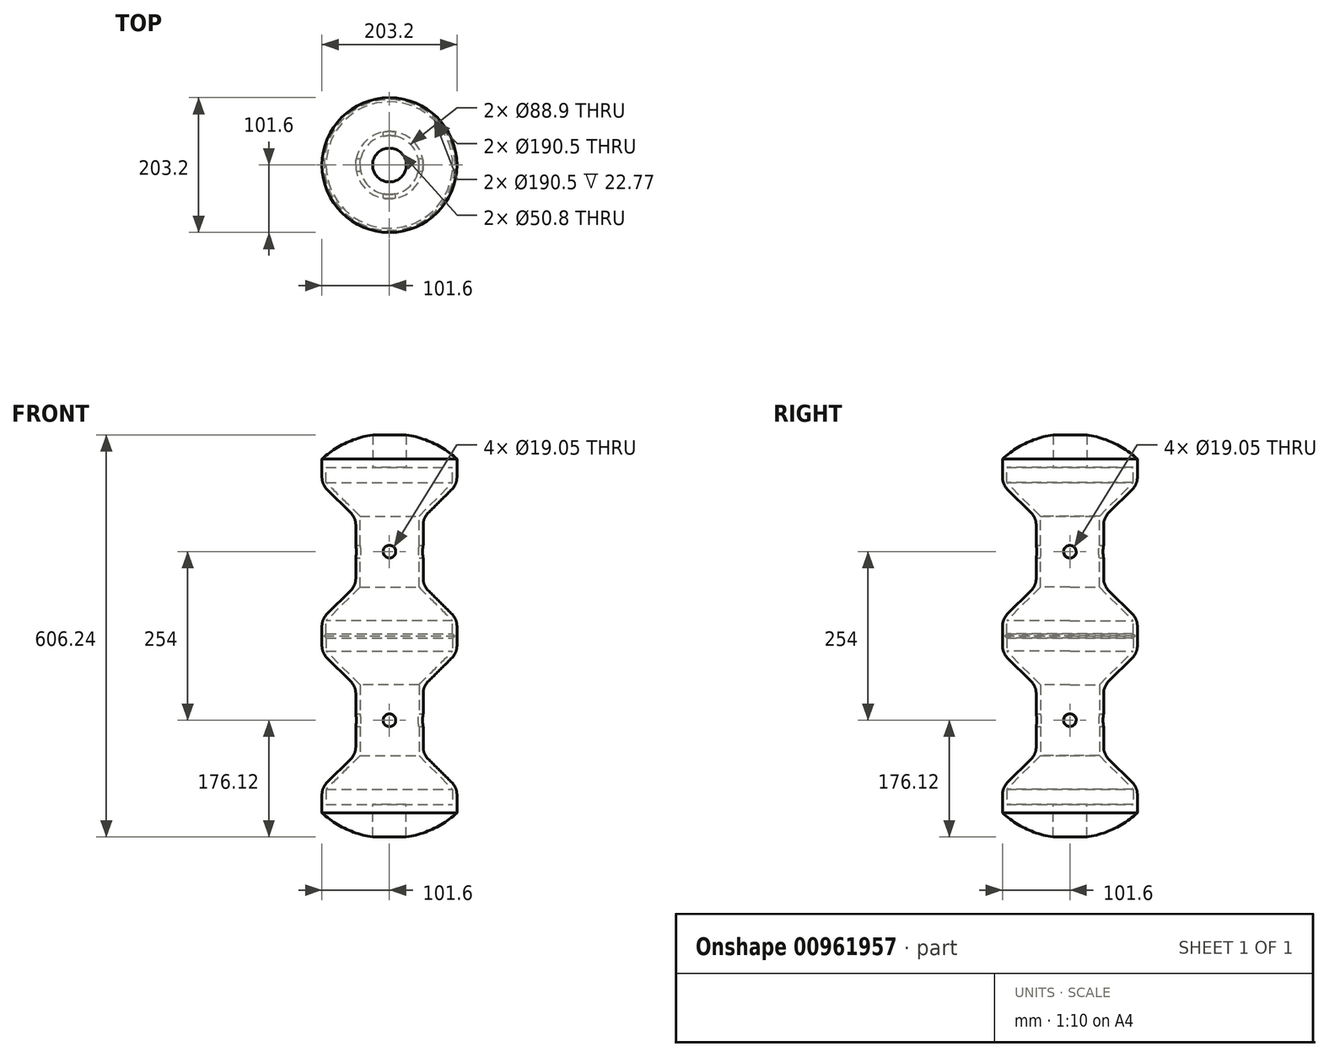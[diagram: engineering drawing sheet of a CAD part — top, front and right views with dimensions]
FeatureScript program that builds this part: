
annotation { "Feature Type Name" : "Feature", "Feature Type Description" : "" }
export const myFeature = defineFeature(function(context is Context, id is Id, definition is map)
    precondition{}
    {
        {
            var Q0;
            Q0=qCreatedBy(makeId("Front.planeOp"),FACE);
            var sketch = newSketch(context, id + "F0", { "sketchPlane" : qUnion([Q0])});
            skLineSegment(sketch, "E0", {"start": v(0, 0) * mm, "end": v(0, 254) * mm});
            skLineSegment(sketch, "E1", {"start": v(0, 254) * mm, "end": v(-101.6, 254) * mm});
            skLineSegment(sketch, "E2", {"start": v(-101.6, 254) * mm, "end": v(-101.6, 228.6) * mm});
            skLineSegment(sketch, "E3", {"start": v(-101.6, 228.6) * mm, "end": v(-50.8, 177.8) * mm});
            skLineSegment(sketch, "E4", {"start": v(0, 127) * mm, "end": v(39.45, 127) * mm, "construction": true});
            skLineSegment(sketch, "E5.MirrorCS", {"start": v(-101.6, 0) * mm, "end": v(-101.6, 25.4) * mm});
            skLineSegment(sketch, "E6.MirrorCS", {"start": v(-101.6, 25.4) * mm, "end": v(-50.8, 76.2) * mm});
            skLineSegment(sketch, "E7.MirrorCS", {"start": v(0, 0) * mm, "end": v(-101.6, 0) * mm});
            skLineSegment(sketch, "E8", {"start": v(-50.8, 177.8) * mm, "end": v(-50.8, 76.2) * mm});
            skSolve(sketch);
        }
        {
            var Q0;
            Q0=makeQuery(id+"F0.imprint","IMPRINT",FACE,{"disambiguationData":[TD([[makeQuery(id+"F0.imprint","IMPRINT",EDGE,{"derivedFrom":sQuery(id+"F0.wireOp",EDGE,"E0")}),1.0]])]});
            var Q1;
            Q1=sQuery(id+"F0.wireOp",EDGE,"E0");
            revolve(context, id + "F1", {"surfaceOperationType" : NewSurfaceOperationType.NEW, "entities" : qUnion([Q0]), "axis" : qUnion([Q1]), "revolveType" : RevolveType.FULL});
        }
        {
            var Q0;
            Q0=makeQuery(id+"F1.opRevolve","SWEPT_FACE",FACE,{"disambiguationData":[OSD([sQuery(id+"F0.wireOp",EDGE,"E1")])]});
            var Q1;
            Q1=makeQuery(id+"F1.opRevolve","SWEPT_BODY",BODY,{"disambiguationData":[OSD([sQuery(id+"F0.wireOp",EDGE,"E0"),sQuery(id+"F0.wireOp",EDGE,"E1"),sQuery(id+"F0.wireOp",EDGE,"E2"),sQuery(id+"F0.wireOp",EDGE,"E3"),sQuery(id+"F0.wireOp",EDGE,"E5.MirrorCS"),sQuery(id+"F0.wireOp",EDGE,"E6.MirrorCS"),sQuery(id+"F0.wireOp",EDGE,"E7.MirrorCS"),sQuery(id+"F0.wireOp",EDGE,"E8")])]});
            shell(context, id + "F2", {"entities" : qUnion([Q0]), "parts" : qUnion([Q1]), "thickness" : 6.35 * mm});
        }
        {
            var Q0;
            Q0=makeQuery(id+"F1.opRevolve","SWEPT_FACE",FACE,{"disambiguationData":[OSD([sQuery(id+"F0.wireOp",EDGE,"E7.MirrorCS")])]});
            var sketch = newSketch(context, id + "F3", { "sketchPlane" : qUnion([Q0])});
            skCircle(sketch, "E9", {"center": v(0, 0) * mm, "radius": 95.25 * mm});
            skSolve(sketch);
        }
        {
            var Q0;
            Q0 = qSketchRegion(id + "F3", true);
            extrude(context, id + "F4", {"entities" : qUnion([Q0]), "operationType" : NewBodyOperationType.REMOVE, "oppositeDirection" : true, "depth" : 6.35 * mm, "offsetDistance" : 25.4 * mm});
        }
        {
            var Q0;
            Q0=qCreatedBy(makeId("Right.planeOp"),FACE);
            var sketch = newSketch(context, id + "F5", { "sketchPlane" : qUnion([Q0])});
            skCircle(sketch, "E10", {"center": v(0, 127) * mm, "radius": 9.53 * mm});
            skSolve(sketch);
        }
        {
            var Q0;
            Q0 = qSketchRegion(id + "F5", true);
            extrude(context, id + "F6", {"entities" : qUnion([Q0]), "operationType" : NewBodyOperationType.REMOVE, "endBound" : BoundingType.SYMMETRIC, "oppositeDirection" : true, "depth" : 254 * mm, "offsetDistance" : 25.4 * mm});
        }
        {
            var Q0;
            Q0=qCreatedBy(makeId("Front.planeOp"),FACE);
            var sketch = newSketch(context, id + "F7", { "sketchPlane" : qUnion([Q0])});
            skCircle(sketch, "E11", {"center": v(0, 127) * mm, "radius": 9.53 * mm});
            skSolve(sketch);
        }
        {
            var Q0;
            Q0 = qSketchRegion(id + "F7", true);
            extrude(context, id + "F8", {"entities" : qUnion([Q0]), "operationType" : NewBodyOperationType.REMOVE, "endBound" : BoundingType.SYMMETRIC, "depth" : 254 * mm, "offsetDistance" : 25.4 * mm});
        }
        {
            var Q0;
            Q0=makeQuery(id+"F1.opRevolve","SWEPT_EDGE",EDGE,{"disambiguationData":[OSD([sQuery(id+"F0.wireOp",EDGE,"E6.MirrorCS"),sQuery(id+"F0.wireOp",EDGE,"E8")])]});
            var Q1;
            Q1=makeQuery(id+"F1.opRevolve","SWEPT_EDGE",EDGE,{"disambiguationData":[OSD([sQuery(id+"F0.wireOp",EDGE,"E5.MirrorCS"),sQuery(id+"F0.wireOp",EDGE,"E6.MirrorCS")])]});
            var Q2;
            Q2=makeQuery(id+"F1.opRevolve","SWEPT_EDGE",EDGE,{"disambiguationData":[OSD([sQuery(id+"F0.wireOp",EDGE,"E2"),sQuery(id+"F0.wireOp",EDGE,"E3")])]});
            var Q3;
            Q3=makeQuery(id+"F1.opRevolve","SWEPT_EDGE",EDGE,{"disambiguationData":[OSD([sQuery(id+"F0.wireOp",EDGE,"E3"),sQuery(id+"F0.wireOp",EDGE,"E8")])]});
            fillet(context, id + "F9", {"entities" : qUnion([Q0, Q1, Q2, Q3]), "radius" : 25.4 * mm, "tangentPropagation" : true, "allowEdgeOverflow" : false});
        }
        {
            var Q0;
            Q0=makeQuery(id+"F2.opShell","OFFSET_EDGE",EDGE,{"disambiguationData":[OSD([sQuery(id+"F0.wireOp",EDGE,"E1"),sQuery(id+"F0.wireOp",EDGE,"E2")])]});
            var Q1;
            Q1=makeQuery(id+"F4.boolean.opBoolean","COPY",EDGE,{"derivedFrom":makeQuery(id+"F4.opExtrude","CAP_EDGE",EDGE,{"disambiguationData":[OSD([sQuery(id+"F3.wireOp",EDGE,"E9")])],"isStart":true})});
            chamfer(context, id + "F10", {"entities" : qUnion([Q0, Q1]), "width" : 3.17 * mm, "tangentPropagation" : true});
        }
        {
            var Q0;
            Q0=qCreatedBy(makeId("Front.planeOp"),FACE);
            var sketch = newSketch(context, id + "F11", { "sketchPlane" : qUnion([Q0])});
            skLineSegment(sketch, "E12", {"start": v(0, 0) * mm, "end": v(0, -50.8) * mm});
            skArc(sketch, "E13", {"start": v(0, -50.8) * mm, "mid": v(54.46, -41.52) * mm, "end": v(101.6, -12.7) * mm});
            skLineSegment(sketch, "E14", {"start": v(0, 0) * mm, "end": v(101.6, 0) * mm});
            skLineSegment(sketch, "E15", {"start": v(101.6, 0) * mm, "end": v(101.6, -12.7) * mm});
            skPoint(sketch, "E16.orphan", {"position": v(101.6, -25.4) * mm});
            skSolve(sketch);
        }
        {
            var Q0;
            Q0=makeQuery(id+"F11.imprint","IMPRINT",FACE,{"disambiguationData":[TD([[makeQuery(id+"F11.imprint","IMPRINT",EDGE,{"derivedFrom":sQuery(id+"F11.wireOp",EDGE,"E12")}),1.0]])]});
            var Q1;
            Q1=sQuery(id+"F11.wireOp",EDGE,"E12");
            revolve(context, id + "F12", {"operationType" : NewBodyOperationType.ADD, "surfaceOperationType" : NewSurfaceOperationType.NEW, "entities" : qUnion([Q0]), "axis" : qUnion([Q1]), "revolveType" : RevolveType.FULL});
        }
        {
            var Q0;
            Q0=makeQuery(id+"F12.opRevolve","SWEPT_FACE",FACE,{"disambiguationData":[OSD([sQuery(id+"F11.wireOp",EDGE,"E14")])]});
            cPlane(context, id + "F13", {"entities" : qUnion([Q0]), "cplaneType" : CPlaneType.OFFSET, "offset" : 50.8 * mm, "oppositeDirection" : true, "width" : 152.4 * mm, "height" : 152.4 * mm});
        }
        {
            var Q0;
            Q0=qCreatedBy(id+"F13.planeOp",FACE);
            var sketch = newSketch(context, id + "F14", { "sketchPlane" : qUnion([Q0])});
            skCircle(sketch, "E17", {"center": v(0, 0) * mm, "radius": 25.4 * mm});
            skSolve(sketch);
        }
        {
            var Q0;
            Q0 = qSketchRegion(id + "F14", true);
            extrude(context, id + "F15", {"entities" : qUnion([Q0]), "operationType" : NewBodyOperationType.REMOVE, "endBound" : BoundingType.SYMMETRIC, "oppositeDirection" : true, "depth" : 304.8 * mm, "offsetDistance" : 25.4 * mm});
        }
        {
            var Q0;
            Q0=makeQuery(id+"F1.opRevolve","SWEPT_FACE",FACE,{"disambiguationData":[OSD([sQuery(id+"F0.wireOp",EDGE,"E1")])]});
            cPlane(context, id + "F16", {"entities" : qUnion([Q0]), "cplaneType" : CPlaneType.OFFSET, "offset" : 0 * mm, "width" : 152.4 * mm, "height" : 152.4 * mm});
        }
        {
            var Q0;
            Q0=makeQuery(id+"F1.opRevolve","SWEPT_BODY",BODY,{"disambiguationData":[OSD([sQuery(id+"F0.wireOp",EDGE,"E0"),sQuery(id+"F0.wireOp",EDGE,"E1"),sQuery(id+"F0.wireOp",EDGE,"E2"),sQuery(id+"F0.wireOp",EDGE,"E3"),sQuery(id+"F0.wireOp",EDGE,"E5.MirrorCS"),sQuery(id+"F0.wireOp",EDGE,"E6.MirrorCS"),sQuery(id+"F0.wireOp",EDGE,"E7.MirrorCS"),sQuery(id+"F0.wireOp",EDGE,"E8")])]});
            var Q1;
            Q1=qCreatedBy(id+"F16.planeOp",FACE);
            mirror(context, id + "F17", {"operationType" : NewBodyOperationType.ADD, "entities" : qUnion([Q0]), "mirrorPlane" : qUnion([Q1])});
        }
    });
